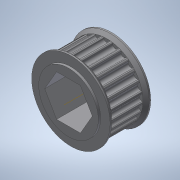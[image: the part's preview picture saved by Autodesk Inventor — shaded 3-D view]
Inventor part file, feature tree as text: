
AUTODESK INVENTOR PART (.ipt)
format: ipt  version: 2022.3 (Build 263350000, 350)  size: 351,232 bytes
history: native  units: in
note: dims shown in document units (in); Inventor stores cm internally (conversion verified against a paired STEP export)
features: sketch x9, extrude x8, fillet x2, pattern_circular x2, mirror x2, chamfer x2, other x1
ambient origin geometry x8: Origin, YZ Plane, XZ Plane, XY Plane, X Axis, Y Axis, Z Axis, Center Point
bodies: Solid1 (feature_tree)
feature tree (26):
  other  "Hex Bore"
  extrude  "HTD Base"  Depth=0.3937in TaperAngle=0.0deg
  extrude  "HTD Base Tooth"  Depth=0.0113in
  fillet  "HTD Base Tooth pt. 2"  [1 undecoded]
  pattern_circular  "HTD Teeth"  Count=25  [1 undecoded]
  extrude  "HTD Flange"  Depth=0.0394in
  mirror  "HTD Flanges"
  chamfer  "HTD Flange Chamfer"  Distance=0.0787in Angle=45.0deg
  extrude  "GT2 Base"  TaperAngle=0.0deg  [1 undecoded]
  extrude  "GT2 Base Tooth"  TaperAngle=0.0deg  [1 undecoded]
  fillet  "GT2 Base Tooth pt. 2"  Radius=0.9099in
  pattern_circular  "GT2 Teeth"  [2 undecoded]
  extrude  "GT2 Flange"  TaperAngle=0.0deg  [1 undecoded]
  mirror  "GT2 Flanges"
  chamfer  "GT2 Flange Chamfer"  Distance=0.0727in
  extrude  "Circle Bore"  Depth=0.03in
  extrude  "Extrusion9"  TaperAngle=0.0deg  [1 undecoded]
  sketch  "Sketch1"  dims[d0=1.5215in d1=0.3937in d2=0.0in]
  sketch  "Sketch2"  dims[d3=0.1208in d5=0.0113in d6=0.0in d7=0.0in]
  sketch  "Sketch3"  dims[d8=0.0169in d9=9.8425in]
  sketch  "Sketch4"  dims[d10=360.0deg d12=0.0394in]
  sketch  "Sketch5"  dims[d13=0.0591in]
  sketch  "Sketch6"  dims[d14=0.0in]
  sketch  "Sketch7"  dims[d15=0.0394in d16=0.0787in d17=45.0deg]
  sketch  "Sketch8"  dims[d18=0.52in d19=0.0in d20=0.0in]
  sketch  "Sketch9"  dims[d21=0.52in d22=0.0in d23=0.0in d24=0.9099in d25=0.3937in d26=0.0in d27=0.0727in d28=0.0075in d29=0.0in d30=0.0in d31=0.0118in d32=9.8425in d33=360.0deg d35=0.0394in d36=0.0591in d37=0.0in d38=0.0394in d39=0.0787in d40=45.0deg d41=0.75in d42=0.03in d43=0.0in]
note: 8 required parameter values undecoded (feature->parameter linkage not recoverable at this tier; creation-order binding heuristic only, values carry confidence <= 0.55)
